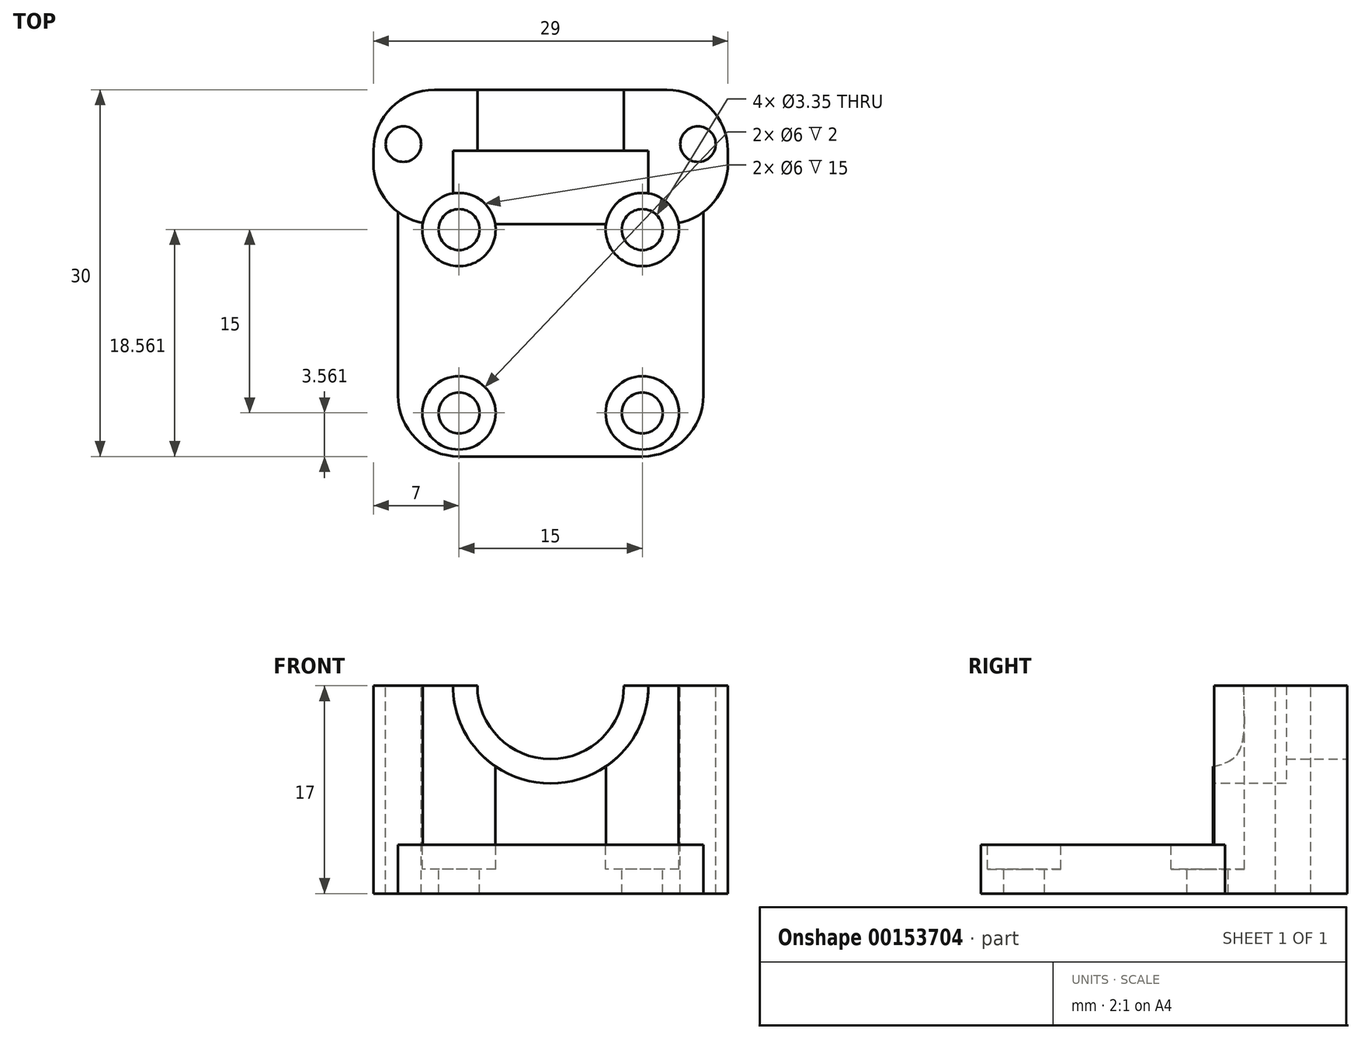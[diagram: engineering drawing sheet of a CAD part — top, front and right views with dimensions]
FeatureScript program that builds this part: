
annotation { "Feature Type Name" : "Feature", "Feature Type Description" : "" }
export const myFeature = defineFeature(function(context is Context, id is Id, definition is map)
    precondition{}
    {
        {
            var Q0;
            Q0=qCreatedBy(makeId("Top.planeOp"),FACE);
            var sketch = newSketch(context, id + "F0", { "sketchPlane" : qUnion([Q0])});
            skLineSegment(sketch, "E0.bottom", {"start": v(0, 0) * mm, "end": v(25, 0) * mm});
            skLineSegment(sketch, "E0.top", {"start": v(0, 30) * mm, "end": v(25, 30) * mm});
            skLineSegment(sketch, "E0.left", {"start": v(0, 0) * mm, "end": v(0, 30) * mm});
            skLineSegment(sketch, "E0.right", {"start": v(25, 0) * mm, "end": v(25, 30) * mm});
            skSolve(sketch);
        }
        {
            var Q0;
            Q0=qSketchRegion(id+"F0",true);
            extrude(context, id + "F1", {"entities" : qUnion([Q0]), "depth" : 4 * mm});
        }
        {
            var Q0;
            Q0=makeQuery(id+"F1.opExtrude","CAP_FACE",FACE,{"disambiguationData":[OSD([sQuery(id+"F0.wireOp",EDGE,"E0.bottom"),sQuery(id+"F0.wireOp",EDGE,"E0.top"),sQuery(id+"F0.wireOp",EDGE,"E0.left"),sQuery(id+"F0.wireOp",EDGE,"E0.right")])],"isStart":false});
            var sketch = newSketch(context, id + "F2", { "sketchPlane" : qUnion([Q0])});
            skCircle(sketch, "E1", {"center": v(5, 18.56) * mm, "radius": 1.68 * mm});
            skCircle(sketch, "E2", {"center": v(20, 18.56) * mm, "radius": 1.68 * mm});
            skCircle(sketch, "E3", {"center": v(5, 3.56) * mm, "radius": 1.68 * mm});
            skCircle(sketch, "E4", {"center": v(20, 3.56) * mm, "radius": 1.68 * mm});
            skLineSegment(sketch, "E5", {"start": v(5, 18.56) * mm, "end": v(0, 18.56) * mm});
            skLineSegment(sketch, "E6", {"start": v(20, 3.56) * mm, "end": v(25, 3.56) * mm});
            skCircle(sketch, "E7", {"center": v(5, 18.56) * mm, "radius": 3 * mm});
            skCircle(sketch, "E8", {"center": v(20, 18.56) * mm, "radius": 3 * mm});
            skCircle(sketch, "E9", {"center": v(5, 3.56) * mm, "radius": 3 * mm});
            skCircle(sketch, "E10", {"center": v(20, 3.56) * mm, "radius": 3 * mm});
            skSolve(sketch);
        }
        {
            var Q0;
            Q0=makeQuery(id+"F2.imprint","IMPRINT",FACE,{"disambiguationData":[TD([[makeQuery(id+"F2.imprint","IMPRINT",EDGE,{"derivedFrom":sQuery(id+"F2.wireOp",EDGE,"E1")}),1.0]])]});
            var Q1;
            Q1=makeQuery(id+"F2.imprint","IMPRINT",FACE,{"disambiguationData":[TD([[makeQuery(id+"F2.imprint","IMPRINT",EDGE,{"derivedFrom":sQuery(id+"F2.wireOp",EDGE,"E2")}),1.0]])]});
            var Q2;
            Q2=makeQuery(id+"F2.imprint","IMPRINT",FACE,{"disambiguationData":[TD([[makeQuery(id+"F2.imprint","IMPRINT",EDGE,{"derivedFrom":sQuery(id+"F2.wireOp",EDGE,"E4")}),1.0]])]});
            var Q3;
            Q3=makeQuery(id+"F2.imprint","IMPRINT",FACE,{"disambiguationData":[TD([[makeQuery(id+"F2.imprint","IMPRINT",EDGE,{"derivedFrom":sQuery(id+"F2.wireOp",EDGE,"E3")}),1.0]])]});
            extrude(context, id + "F3", {"entities" : qUnion([Q0, Q1, Q2, Q3]), "operationType" : NewBodyOperationType.REMOVE, "oppositeDirection" : true, "depth" : 25 * mm});
        }
        {
            var Q0;
            Q0=makeQuery(id+"F1.opExtrude","CAP_FACE",FACE,{"disambiguationData":[OSD([sQuery(id+"F0.wireOp",EDGE,"E0.bottom"),sQuery(id+"F0.wireOp",EDGE,"E0.top"),sQuery(id+"F0.wireOp",EDGE,"E0.left"),sQuery(id+"F0.wireOp",EDGE,"E0.right")])],"isStart":false});
            var sketch = newSketch(context, id + "F4", { "sketchPlane" : qUnion([Q0])});
            skLineSegment(sketch, "E11.bottom", {"start": v(0, 30) * mm, "end": v(25, 30) * mm});
            skLineSegment(sketch, "E11.top", {"start": v(0, 19) * mm, "end": v(25, 19) * mm});
            skLineSegment(sketch, "E11.left", {"start": v(0, 30) * mm, "end": v(0, 19) * mm});
            skLineSegment(sketch, "E11.right", {"start": v(25, 30) * mm, "end": v(25, 19) * mm});
            skSolve(sketch);
        }
        {
            var Q0;
            Q0=qSketchRegion(id+"F4",true);
            extrude(context, id + "F5", {"entities" : qUnion([Q0]), "operationType" : NewBodyOperationType.ADD, "depth" : 13 * mm});
        }
        {
            var Q0;
            Q0=makeQuery(id+"F5.boolean.opBoolean","MERGE",FACE,{"derivedFrom":[makeQuery(id+"F1.opExtrude","SWEPT_FACE",FACE,{"disambiguationData":[OSD([sQuery(id+"F0.wireOp",EDGE,"E0.top")])]}),makeQuery(id+"F5.opExtrude","SWEPT_FACE",FACE,{"disambiguationData":[OSD([sQuery(id+"F4.wireOp",EDGE,"E11.bottom")])]})]});
            var sketch = newSketch(context, id + "F6", { "sketchPlane" : qUnion([Q0])});
            skCircle(sketch, "E12", {"center": v(-12.5, 17) * mm, "radius": 6 * mm});
            skSolve(sketch);
        }
        {
            var Q0;
            {var subQ0=makeQuery(id+"F5.opExtrude","CAP_EDGE",EDGE,{"disambiguationData":[OSD([sQuery(id+"F4.wireOp",EDGE,"E11.bottom")])],"isStart":false});var subQ1=sQuery(id+"F6.wireOp",EDGE,"E12");var subQ3=makeQuery(id+"F6.imprint","INTERSECT",VERTEX,{"disambiguationData":[OD(0.0)],"derivedFrom":[subQ0,subQ1]});Q0=makeQuery(id+"F6.imprint","IMPRINT",FACE,{"disambiguationData":[TD([[makeQuery(id+"F6.imprint","IMPRINT",EDGE,{"disambiguationData":[TD([[subQ3,1.0]])],"derivedFrom":subQ1}),1.0]])]});}
            extrude(context, id + "F7", {"entities" : qUnion([Q0]), "operationType" : NewBodyOperationType.REMOVE, "oppositeDirection" : true, "depth" : 6 * mm});
        }
        {
            var Q0;
            Q0=makeQuery(id+"F5.opExtrude","SWEPT_FACE",FACE,{"disambiguationData":[OSD([sQuery(id+"F4.wireOp",EDGE,"E11.top")])]});
            var sketch = newSketch(context, id + "F8", { "sketchPlane" : qUnion([Q0])});
            skCircle(sketch, "E13", {"center": v(12.5, 17) * mm, "radius": 8 * mm});
            skSolve(sketch);
        }
        {
            var Q0;
            Q0=qSketchRegion(id+"F8",true);
            extrude(context, id + "F9", {"entities" : qUnion([Q0]), "operationType" : NewBodyOperationType.REMOVE, "oppositeDirection" : true, "depth" : 6 * mm});
        }
        {
            var Q0;
            Q0=makeQuery(id+"F2.imprint","IMPRINT",FACE,{"disambiguationData":[TD([[makeQuery(id+"F2.imprint","IMPRINT",EDGE,{"derivedFrom":sQuery(id+"F2.wireOp",EDGE,"E1")}),-1.0]])]});
            var Q1;
            Q1=makeQuery(id+"F2.imprint","IMPRINT",FACE,{"disambiguationData":[TD([[makeQuery(id+"F2.imprint","IMPRINT",EDGE,{"derivedFrom":sQuery(id+"F2.wireOp",EDGE,"E2")}),-1.0]])]});
            var Q2;
            Q2=makeQuery(id+"F2.imprint","IMPRINT",FACE,{"disambiguationData":[TD([[makeQuery(id+"F2.imprint","IMPRINT",EDGE,{"derivedFrom":sQuery(id+"F2.wireOp",EDGE,"E4")}),-1.0]])]});
            var Q3;
            Q3=makeQuery(id+"F2.imprint","IMPRINT",FACE,{"disambiguationData":[TD([[makeQuery(id+"F2.imprint","IMPRINT",EDGE,{"derivedFrom":sQuery(id+"F2.wireOp",EDGE,"E3")}),-1.0]])]});
            extrude(context, id + "F10", {"entities" : qUnion([Q0, Q1, Q2, Q3]), "operationType" : NewBodyOperationType.REMOVE, "oppositeDirection" : true, "depth" : 2 * mm});
        }
        {
            var Q0;
            Q0=makeQuery(id+"F5.boolean.opBoolean","MERGE",FACE,{"derivedFrom":[makeQuery(id+"F1.opExtrude","SWEPT_FACE",FACE,{"disambiguationData":[OSD([sQuery(id+"F0.wireOp",EDGE,"E0.left")])]}),makeQuery(id+"F5.opExtrude","SWEPT_FACE",FACE,{"disambiguationData":[OSD([sQuery(id+"F4.wireOp",EDGE,"E11.left")])]})]});
            var sketch = newSketch(context, id + "F11", { "sketchPlane" : qUnion([Q0])});
            skLineSegment(sketch, "E14.bottom", {"start": v(-30, 0) * mm, "end": v(-19, 0) * mm});
            skLineSegment(sketch, "E14.top", {"start": v(-30, 17) * mm, "end": v(-19, 17) * mm});
            skLineSegment(sketch, "E14.left", {"start": v(-30, 0) * mm, "end": v(-30, 17) * mm});
            skLineSegment(sketch, "E14.right", {"start": v(-19, 0) * mm, "end": v(-19, 17) * mm});
            skSolve(sketch);
        }
        {
            var Q0;
            Q0 = qSketchRegion(id + "F11", true);
            extrude(context, id + "F12", {"entities" : qUnion([Q0]), "operationType" : NewBodyOperationType.ADD, "depth" : 2 * mm});
        }
        {
            var Q0;
            Q0=makeQuery(id+"F1.opExtrude","SWEPT_EDGE",EDGE,{"disambiguationData":[OSD([sQuery(id+"F0.wireOp",EDGE,"E0.bottom"),sQuery(id+"F0.wireOp",EDGE,"E0.left")])]});
            var Q1;
            Q1=makeQuery(id+"F1.opExtrude","SWEPT_EDGE",EDGE,{"disambiguationData":[OSD([sQuery(id+"F0.wireOp",EDGE,"E0.bottom"),sQuery(id+"F0.wireOp",EDGE,"E0.right")])]});
            fillet(context, id + "F13", {"entities" : qUnion([Q0, Q1]), "radius" : 5 * mm, "tangentPropagation" : true, "allowEdgeOverflow" : false});
        }
        {
            var Q0;
            Q0=makeQuery(id+"F5.boolean.opBoolean","MERGE",FACE,{"derivedFrom":[makeQuery(id+"F1.opExtrude","SWEPT_FACE",FACE,{"disambiguationData":[OSD([sQuery(id+"F0.wireOp",EDGE,"E0.right")])]}),makeQuery(id+"F5.opExtrude","SWEPT_FACE",FACE,{"disambiguationData":[OSD([sQuery(id+"F4.wireOp",EDGE,"E11.right")])]})]});
            var sketch = newSketch(context, id + "F14", { "sketchPlane" : qUnion([Q0])});
            skLineSegment(sketch, "E15.bottom", {"start": v(30, 0) * mm, "end": v(19, 0) * mm});
            skLineSegment(sketch, "E15.top", {"start": v(30, 17) * mm, "end": v(19, 17) * mm});
            skLineSegment(sketch, "E15.left", {"start": v(30, 0) * mm, "end": v(30, 17) * mm});
            skLineSegment(sketch, "E15.right", {"start": v(19, 0) * mm, "end": v(19, 17) * mm});
            skSolve(sketch);
        }
        {
            var Q0;
            Q0=qSketchRegion(id+"F14",true);
            extrude(context, id + "F15", {"entities" : qUnion([Q0]), "operationType" : NewBodyOperationType.ADD, "depth" : 2 * mm});
        }
        {
            var Q0;
            Q0=qSketchRegion(id+"F14",true);
            extrude(context, id + "F16", {"entities" : qUnion([Q0]), "operationType" : NewBodyOperationType.ADD, "depth" : 2 * mm});
        }
        {
            var Q0;
            {var subQ0=sQuery(id+"F4.wireOp",EDGE,"E11.bottom");var subQ1=sQuery(id+"F4.wireOp",EDGE,"E11.top");var subQ2=sQuery(id+"F4.wireOp",EDGE,"E11.left");Q0=makeQuery(id+"F9.boolean.opBoolean","SPLIT",FACE,{"disambiguationData":[TD([makeQuery(id+"F1.opExtrude","SWEPT_FACE",FACE,{"disambiguationData":[OSD([sQuery(id+"F0.wireOp",EDGE,"E0.left")])]})])],"derivedFrom":makeQuery(id+"F5.opExtrude","CAP_FACE",FACE,{"disambiguationData":[OSD([subQ0,subQ1,subQ2,sQuery(id+"F4.wireOp",EDGE,"E11.right")])],"isStart":false})});}
            var sketch = newSketch(context, id + "F17", { "sketchPlane" : qUnion([Q0])});
            skCircle(sketch, "E16", {"center": v(0.45, 25.55) * mm, "radius": 1.45 * mm});
            skCircle(sketch, "E17", {"center": v(24.55, 25.55) * mm, "radius": 1.45 * mm});
            skSolve(sketch);
        }
        {
            var Q0;
            Q0=qSketchRegion(id+"F17",true);
            extrude(context, id + "F18", {"entities" : qUnion([Q0]), "operationType" : NewBodyOperationType.REMOVE, "oppositeDirection" : true, "depth" : 25 * mm});
        }
        {
            var Q0;
            Q0=makeQuery(id+"F12.opExtrude","CAP_EDGE",EDGE,{"disambiguationData":[OSD([sQuery(id+"F11.wireOp",EDGE,"E14.left")])],"isStart":false});
            var Q1;
            Q1=makeQuery(id+"F12.opExtrude","CAP_EDGE",EDGE,{"disambiguationData":[OSD([sQuery(id+"F11.wireOp",EDGE,"E14.right")])],"isStart":false});
            var Q2;
            Q2=makeQuery(id+"F15.opExtrude","CAP_EDGE",EDGE,{"disambiguationData":[OSD([sQuery(id+"F14.wireOp",EDGE,"E15.right")])],"isStart":false});
            var Q3;
            Q3=makeQuery(id+"F15.opExtrude","CAP_EDGE",EDGE,{"disambiguationData":[OSD([sQuery(id+"F14.wireOp",EDGE,"E15.left")])],"isStart":false});
            fillet(context, id + "F19", {"entities" : qUnion([Q0, Q1, Q2, Q3]), "radius" : 5 * mm, "tangentPropagation" : true, "allowEdgeOverflow" : false});
        }
        {
            var Q0;
            Q0=makeQuery(id+"F2.imprint","IMPRINT",FACE,{"disambiguationData":[TD([[makeQuery(id+"F2.imprint","IMPRINT",EDGE,{"derivedFrom":sQuery(id+"F2.wireOp",EDGE,"E1")}),-1.0]])]});
            var Q1;
            Q1=makeQuery(id+"F2.imprint","IMPRINT",FACE,{"disambiguationData":[TD([[makeQuery(id+"F2.imprint","IMPRINT",EDGE,{"derivedFrom":sQuery(id+"F2.wireOp",EDGE,"E2")}),-1.0]])]});
            var Q2;
            Q2=makeQuery(id+"F2.imprint","IMPRINT",FACE,{"disambiguationData":[TD([[makeQuery(id+"F2.imprint","IMPRINT",EDGE,{"derivedFrom":sQuery(id+"F2.wireOp",EDGE,"E1")}),1.0]])]});
            var Q3;
            Q3=makeQuery(id+"F2.imprint","IMPRINT",FACE,{"disambiguationData":[TD([[makeQuery(id+"F2.imprint","IMPRINT",EDGE,{"derivedFrom":sQuery(id+"F2.wireOp",EDGE,"E2")}),1.0]])]});
            extrude(context, id + "F20", {"entities" : qUnion([Q0, Q1, Q2, Q3]), "operationType" : NewBodyOperationType.REMOVE, "depth" : 25 * mm});
        }
    });
